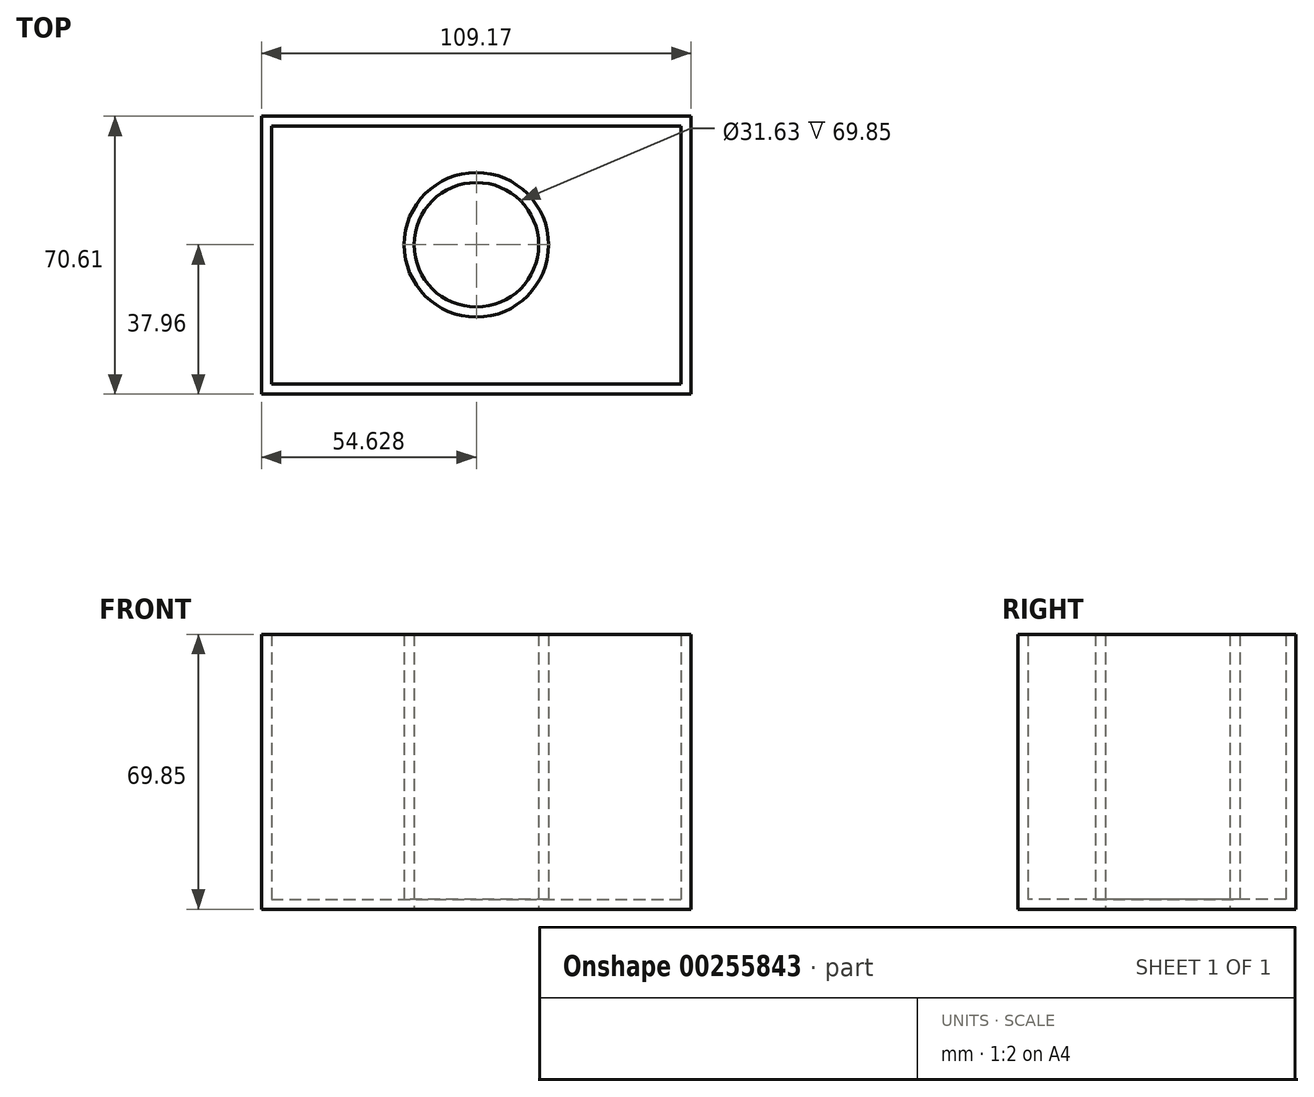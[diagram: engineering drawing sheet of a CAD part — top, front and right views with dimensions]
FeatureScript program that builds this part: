
annotation { "Feature Type Name" : "Feature", "Feature Type Description" : "" }
export const myFeature = defineFeature(function(context is Context, id is Id, definition is map)
    precondition{}
    {
        {
            var Q0;
            Q0=qCreatedBy(makeId("Top.planeOp"),FACE);
            var sketch = newSketch(context, id + "F0", { "sketchPlane" : qUnion([Q0])});
            skLineSegment(sketch, "E0.bottom", {"start": v(-71, 26.36) * mm, "end": v(38.18, 26.36) * mm});
            skLineSegment(sketch, "E0.top", {"start": v(-71, -44.25) * mm, "end": v(38.18, -44.25) * mm});
            skLineSegment(sketch, "E0.left", {"start": v(-71, 26.36) * mm, "end": v(-71, -44.25) * mm});
            skLineSegment(sketch, "E0.right", {"start": v(38.18, 26.36) * mm, "end": v(38.18, -44.25) * mm});
            skCircle(sketch, "E1", {"center": v(-16.36, -6.29) * mm, "radius": 15.82 * mm});
            skSolve(sketch);
        }
        {
            var Q0;
            Q0 = qSketchRegion(id + "F0", true);
            extrude(context, id + "F1", {"entities" : qUnion([Q0]), "depth" : 69.85 * mm});
        }
        {
            var Q0;
            Q0=makeQuery(id+"F1.opExtrude","CAP_FACE",FACE,{"disambiguationData":[OSD([sQuery(id+"F0.wireOp",EDGE,"E0.bottom"),sQuery(id+"F0.wireOp",EDGE,"E0.top"),sQuery(id+"F0.wireOp",EDGE,"E0.left"),sQuery(id+"F0.wireOp",EDGE,"E0.right"),sQuery(id+"F0.wireOp",EDGE,"E1")])],"isStart":false});
            shell(context, id + "F2", {"entities" : qUnion([Q0]), "thickness" : 2.54 * mm});
        }
    });
